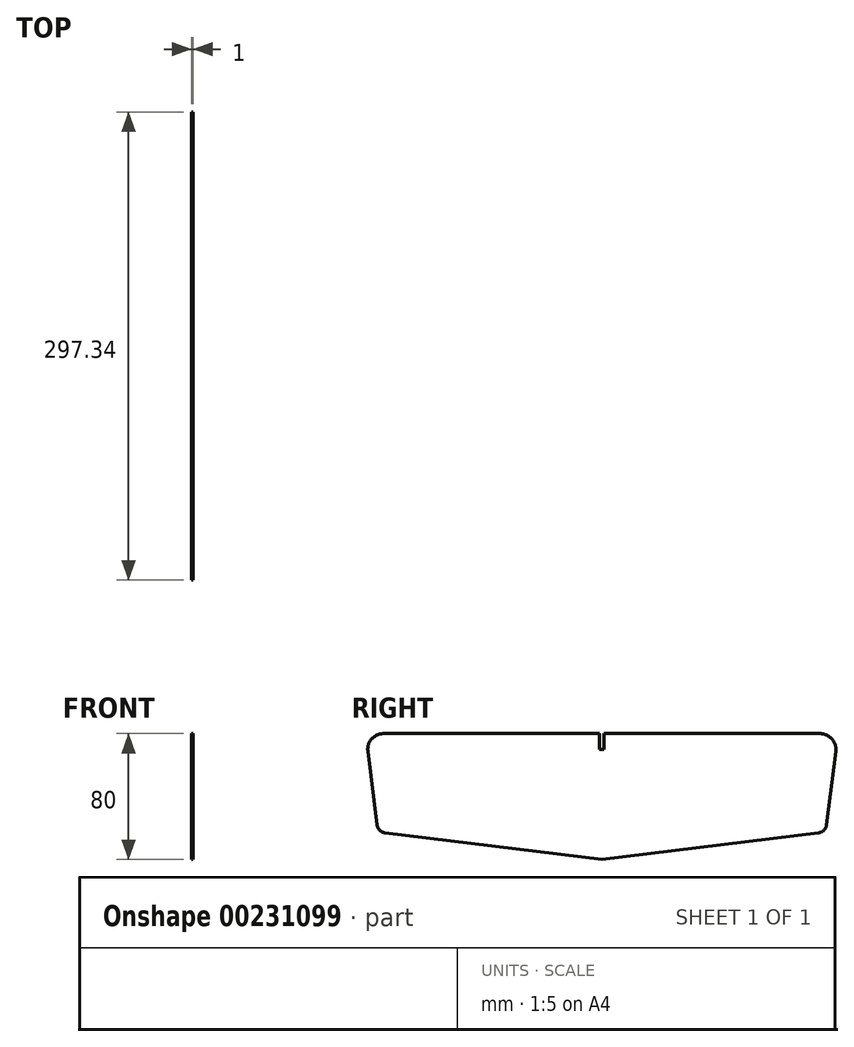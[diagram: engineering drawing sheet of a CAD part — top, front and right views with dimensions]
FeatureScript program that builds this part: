
annotation { "Feature Type Name" : "Feature", "Feature Type Description" : "" }
export const myFeature = defineFeature(function(context is Context, id is Id, definition is map)
    precondition{}
    {
        {
            var Q0;
            Q0=qCreatedBy(makeId("Right.planeOp"),FACE);
            var sketch = newSketch(context, id + "F0", { "sketchPlane" : qUnion([Q0])});
            skLineSegment(sketch, "E0", {"start": v(-155.04, -7.11) * mm, "end": v(-17.71, -7.11) * mm});
            skLineSegment(sketch, "E1", {"start": v(-164.97, -18.35) * mm, "end": v(-159.14, -64.95) * mm});
            skLineSegment(sketch, "E2", {"start": v(132.22, -18.35) * mm, "end": v(126.4, -64.95) * mm});
            skArc(sketch, "E3", {"start": v(132.22, -18.35) * mm, "mid": v(129.8, -10.5) * mm, "end": v(122.3, -7.11) * mm});
            skArc(sketch, "E4", {"start": v(-155.04, -7.11) * mm, "mid": v(-162.54, -10.5) * mm, "end": v(-164.97, -18.35) * mm});
            skLineSegment(sketch, "E5", {"start": v(-15.03, -7.11) * mm, "end": v(-15.03, -17.11) * mm});
            skLineSegment(sketch, "E6", {"start": v(-17.71, -7.11) * mm, "end": v(-17.71, -17.11) * mm});
            skLineSegment(sketch, "E7", {"start": v(-15.03, -7.11) * mm, "end": v(122.3, -7.11) * mm});
            skLineSegment(sketch, "E8", {"start": v(-17.71, -17.11) * mm, "end": v(-15.03, -17.11) * mm});
            skLineSegment(sketch, "E9", {"start": v(-16.37, -87.11) * mm, "end": v(-153.92, -70.16) * mm});
            skLineSegment(sketch, "E10", {"start": v(-16.37, -87.11) * mm, "end": v(121.18, -70.16) * mm});
            skArc(sketch, "E11", {"start": v(-159.14, -64.95) * mm, "mid": v(-157.43, -68.45) * mm, "end": v(-153.92, -70.16) * mm});
            skArc(sketch, "E12", {"start": v(121.18, -70.16) * mm, "mid": v(124.68, -68.45) * mm, "end": v(126.4, -64.95) * mm});
            skSolve(sketch);
        }
        {
            var Q0;
            Q0 = qSketchRegion(id + "F0", true);
            extrude(context, id + "F1", {"entities" : qUnion([Q0]), "depth" : 1 * mm});
        }
    });
